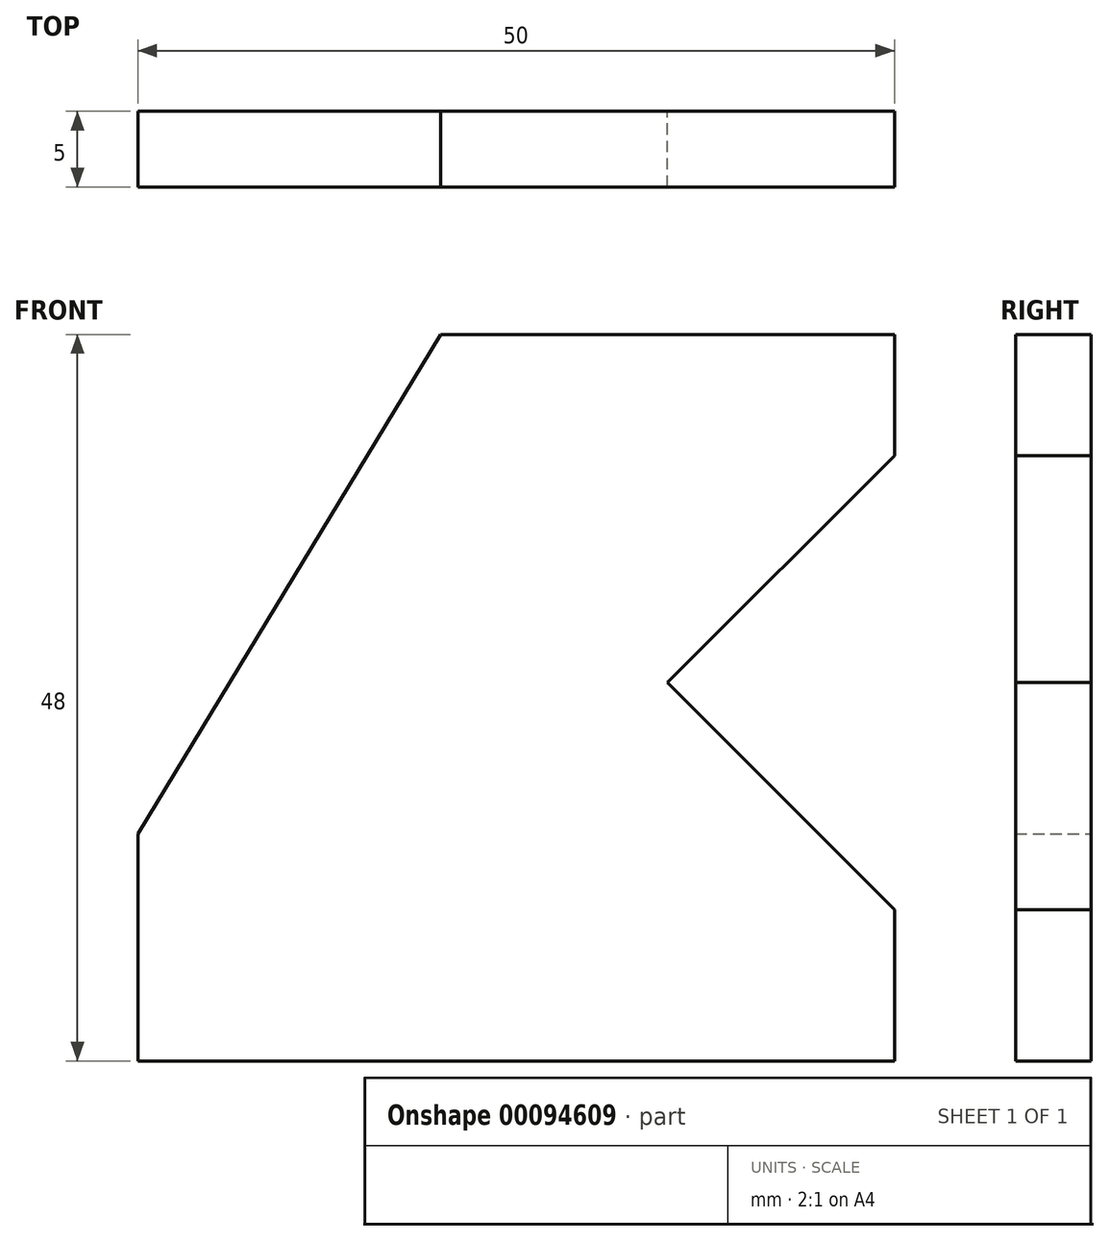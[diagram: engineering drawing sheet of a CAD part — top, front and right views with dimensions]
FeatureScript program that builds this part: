
annotation { "Feature Type Name" : "Feature", "Feature Type Description" : "" }
export const myFeature = defineFeature(function(context is Context, id is Id, definition is map)
    precondition{}
    {
        {
            var Q0;
            Q0=qCreatedBy(makeId("Front.planeOp"),FACE);
            var sketch = newSketch(context, id + "F0", { "sketchPlane" : qUnion([Q0])});
            skLineSegment(sketch, "E0", {"start": v(-14.78, 0) * mm, "end": v(11.41, 0) * mm, "construction": true});
            skLineSegment(sketch, "E1", {"start": v(0, 0) * mm, "end": v(15, 15) * mm});
            skLineSegment(sketch, "E2.MirrorCS", {"start": v(0, 0) * mm, "end": v(15, -15) * mm});
            skLineSegment(sketch, "E3", {"start": v(15, -15) * mm, "end": v(15, -25) * mm});
            skLineSegment(sketch, "E4", {"start": v(15, -25) * mm, "end": v(-35, -25) * mm});
            skLineSegment(sketch, "E5", {"start": v(-35, -25) * mm, "end": v(-35, -10) * mm});
            skLineSegment(sketch, "E6", {"start": v(15, 15) * mm, "end": v(15, 23) * mm});
            skLineSegment(sketch, "E7", {"start": v(15, 23) * mm, "end": v(-15, 23) * mm});
            skLineSegment(sketch, "E8", {"start": v(-15, 23) * mm, "end": v(-35, -10) * mm});
            skSolve(sketch);
        }
        {
            var Q0;
            Q0 = qSketchRegion(id + "F0", true);
            extrude(context, id + "F1", {"entities" : qUnion([Q0]), "depth" : 5 * mm});
        }
    });
